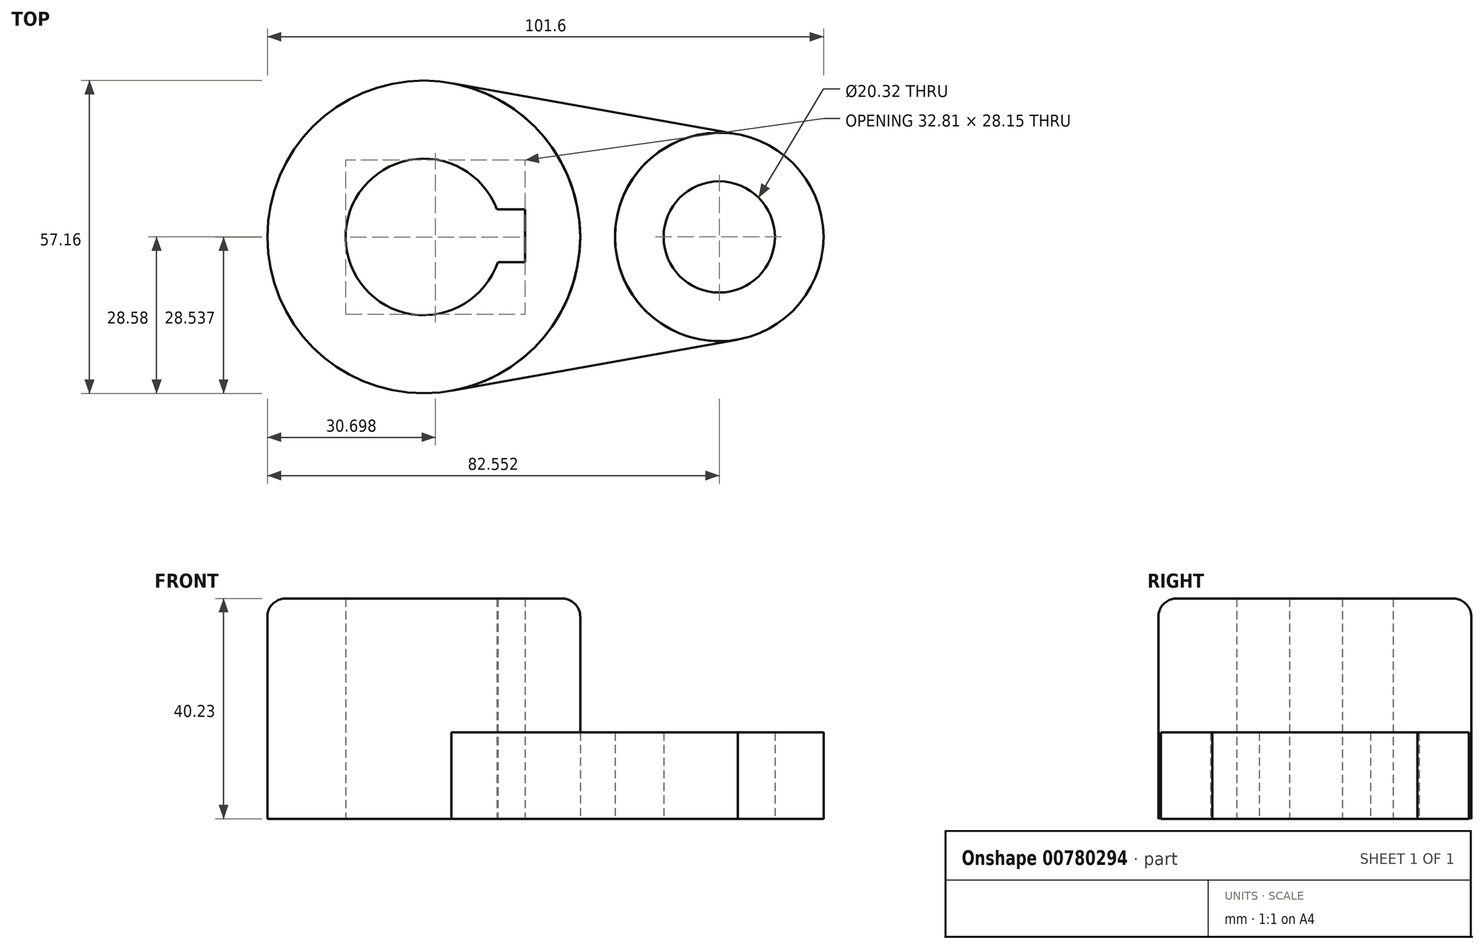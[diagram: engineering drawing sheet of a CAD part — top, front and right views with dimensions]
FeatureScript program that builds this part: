
annotation { "Feature Type Name" : "Feature", "Feature Type Description" : "" }
export const myFeature = defineFeature(function(context is Context, id is Id, definition is map)
    precondition{}
    {
        {
            var Q0;
            Q0=qCreatedBy(makeId("Top.planeOp"),FACE);
            var sketch = newSketch(context, id + "F0", { "sketchPlane" : qUnion([Q0])});
            skArc(sketch, "E0", {"start": v(-8.06, 5.06) * mm, "mid": v(-35.7, -0.25) * mm, "end": v(-7.9, -4.6) * mm});
            skCircle(sketch, "E1", {"center": v(32.55, 0) * mm, "radius": 10.16 * mm});
            skCircle(sketch, "E2", {"center": v(-21.42, 0) * mm, "radius": 28.58 * mm});
            skCircle(sketch, "E3", {"center": v(32.55, 0) * mm, "radius": 19.05 * mm});
            skLineSegment(sketch, "E4.bottom", {"start": v(-8.06, 5.06) * mm, "end": v(-2.9, 5.06) * mm});
            skLineSegment(sketch, "E4.top", {"start": v(-6.59, -4.6) * mm, "end": v(-2.9, -4.6) * mm});
            skLineSegment(sketch, "E4.right", {"start": v(-2.9, 5.06) * mm, "end": v(-2.9, -4.6) * mm});
            skLineSegment(sketch, "E5", {"start": v(-16.38, -28.13) * mm, "end": v(35.91, -18.75) * mm});
            skLineSegment(sketch, "E6", {"start": v(-16.38, 28.13) * mm, "end": v(35.91, 18.75) * mm});
            skLineSegment(sketch, "E7", {"start": v(-7.9, -4.6) * mm, "end": v(-6.59, -4.6) * mm});
            skSolve(sketch);
        }
        {
            var Q0;
            Q0=makeQuery(id+"F0.imprint","IMPRINT",FACE,{"disambiguationData":[TD([[makeQuery(id+"F0.imprint","IMPRINT",EDGE,{"derivedFrom":sQuery(id+"F0.wireOp",EDGE,"E0")}),-1.0]])]});
            extrude(context, id + "F1", {"entities" : qUnion([Q0]), "depth" : 40.23 * mm, "offsetDistance" : 25.4 * mm});
        }
        {
            var Q0;
            Q0=makeQuery(id+"F0.imprint","IMPRINT",FACE,{"disambiguationData":[TD([[makeQuery(id+"F0.imprint","IMPRINT",EDGE,{"derivedFrom":sQuery(id+"F0.wireOp",EDGE,"E1")}),-1.0]])]});
            extrude(context, id + "F2", {"entities" : qUnion([Q0]), "depth" : 15.77 * mm, "offsetDistance" : 25.4 * mm});
        }
        {
            var Q0;
            {var subQ0=sQuery(id+"F0.wireOp",EDGE,"E5");Q0=makeQuery(id+"F0.imprint","IMPRINT",FACE,{"disambiguationData":[TD([[makeQuery(id+"F0.imprint","IMPRINT",EDGE,{"derivedFrom":subQ0}),1.0]])]});}
            extrude(context, id + "F3", {"entities" : qUnion([Q0]), "depth" : 15.77 * mm, "offsetDistance" : 25.4 * mm});
        }
        {
            var Q0;
            Q0=makeQuery(id+"F1.opExtrude","CAP_EDGE",EDGE,{"disambiguationData":[OSD([sQuery(id+"F0.wireOp",EDGE,"E2")])],"isStart":false});
            fillet(context, id + "F4", {"entities" : qUnion([Q0]), "radius" : 3.3 * mm, "tangentPropagation" : true, "allowEdgeOverflow" : false});
        }
    });
